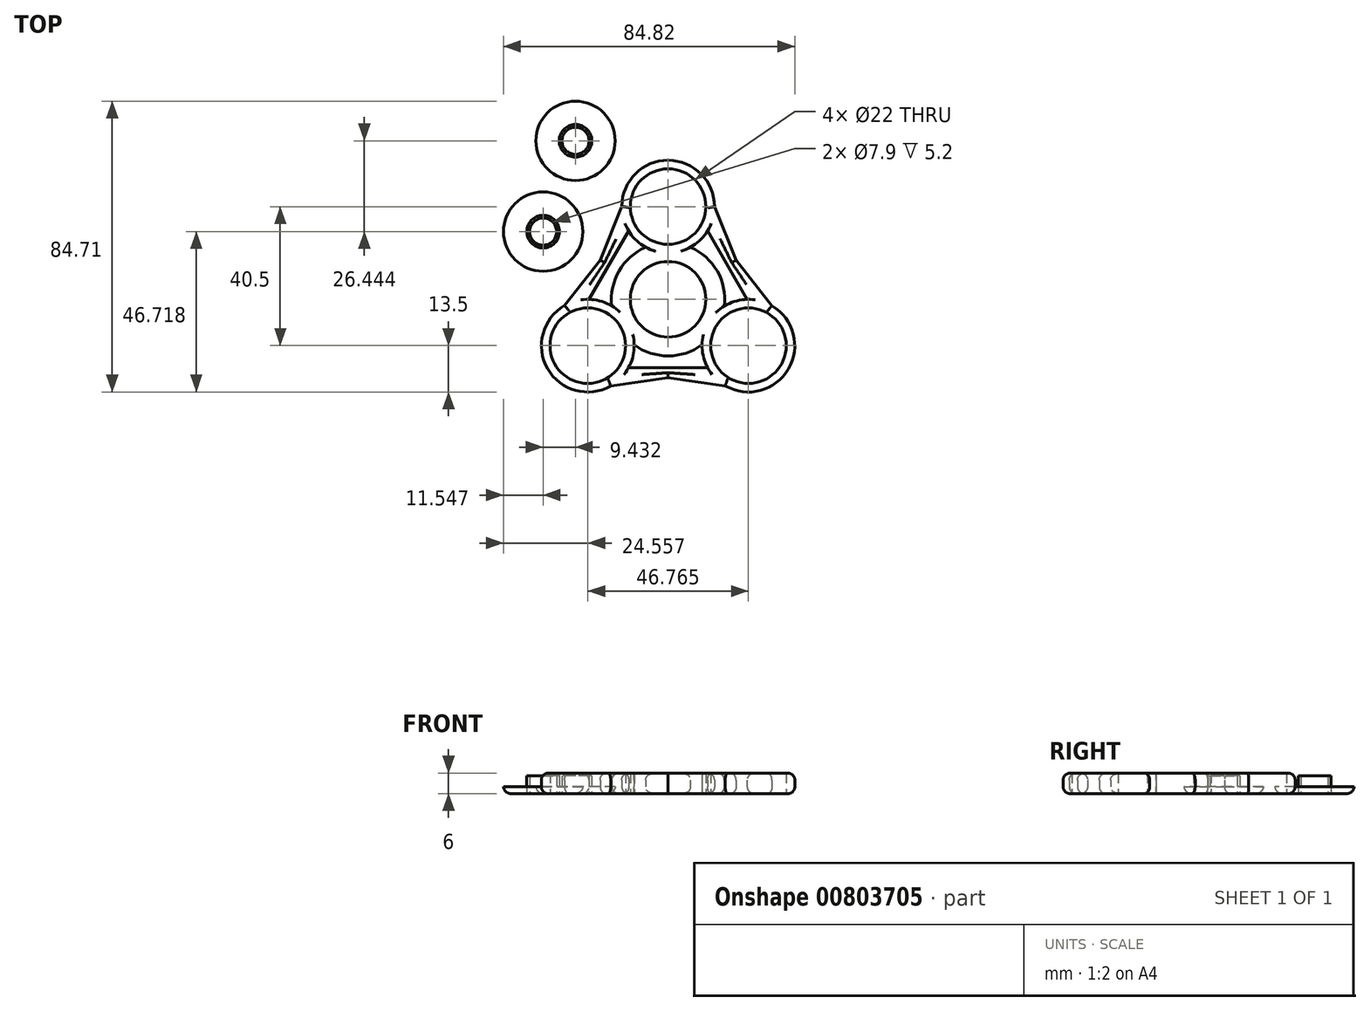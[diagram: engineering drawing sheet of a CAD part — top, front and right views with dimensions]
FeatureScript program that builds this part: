
annotation { "Feature Type Name" : "Feature", "Feature Type Description" : "" }
export const myFeature = defineFeature(function(context is Context, id is Id, definition is map)
    precondition{}
    {
        {
            var Q0;
            Q0=qCreatedBy(makeId("Top.planeOp"),FACE);
            var sketch = newSketch(context, id + "F0", { "sketchPlane" : qUnion([Q0])});
            skCircle(sketch, "E0", {"center": v(0, 0) * mm, "radius": 11 * mm});
            skArc(sketch, "E1", {"start": v(-6.5, 15.17) * mm, "mid": v(-14.29, 8.25) * mm, "end": v(-16.38, -1.96) * mm});
            skCircle(sketch, "E2", {"center": v(0, 27) * mm, "radius": 11 * mm});
            skArc(sketch, "E3", {"start": v(6.5, 15.17) * mm, "mid": v(9.3, 17.22) * mm, "end": v(11.5, 19.92) * mm});
            skLineSegment(sketch, "E4", {"start": v(-13.5, 27.1) * mm, "end": v(-19.78, 11.42) * mm});
            skLineSegment(sketch, "E5", {"start": v(-11.5, 19.92) * mm, "end": v(-17.25, 9.96) * mm});
            skLineSegment(sketch, "E6", {"start": v(13.5, 27) * mm, "end": v(19.78, 11.42) * mm});
            skLineSegment(sketch, "E7", {"start": v(11.5, 19.92) * mm, "end": v(17.25, 9.96) * mm});
            skArc(sketch, "E8.trimOffspring", {"start": v(13.5, 27) * mm, "mid": v(0.05, 40.5) * mm, "end": v(-13.5, 27.1) * mm});
            skArc(sketch, "E9.trimOffspring", {"start": v(-11.5, 19.92) * mm, "mid": v(-9.3, 17.22) * mm, "end": v(-6.5, 15.17) * mm});
            skArc(sketch, "E10.1.0", {"start": v(-30.13, -1.8) * mm, "mid": v(-35.1, -20.2) * mm, "end": v(-16.72, -25.24) * mm});
            skLineSegment(sketch, "E10.1.1", {"start": v(-30.13, -1.8) * mm, "end": v(-19.78, 11.42) * mm});
            skLineSegment(sketch, "E10.1.2", {"start": v(-23, 0) * mm, "end": v(-17.25, 9.96) * mm});
            skArc(sketch, "E10.1.3", {"start": v(-16.38, -1.96) * mm, "mid": v(-19.57, -0.55) * mm, "end": v(-23, 0) * mm});
            skArc(sketch, "E10.1.4", {"start": v(-11.5, -19.92) * mm, "mid": v(-10.26, -16.67) * mm, "end": v(-9.89, -13.21) * mm});
            skLineSegment(sketch, "E10.1.5", {"start": v(-11.5, -19.92) * mm, "end": v(0, -19.92) * mm});
            skLineSegment(sketch, "E10.1.6", {"start": v(-16.72, -25.24) * mm, "end": v(0, -22.84) * mm});
            skCircle(sketch, "E10.1.7", {"center": v(-23.38, -13.5) * mm, "radius": 11 * mm});
            skArc(sketch, "E10.2.0", {"start": v(16.63, -25.2) * mm, "mid": v(35.05, -20.3) * mm, "end": v(30.22, -1.86) * mm});
            skLineSegment(sketch, "E10.2.1", {"start": v(16.63, -25.2) * mm, "end": v(0, -22.84) * mm});
            skLineSegment(sketch, "E10.2.2", {"start": v(11.5, -19.92) * mm, "end": v(0, -19.92) * mm});
            skArc(sketch, "E10.2.3", {"start": v(9.89, -13.21) * mm, "mid": v(10.26, -16.67) * mm, "end": v(11.5, -19.92) * mm});
            skArc(sketch, "E10.2.4", {"start": v(23, 0) * mm, "mid": v(19.57, -0.55) * mm, "end": v(16.38, -1.96) * mm});
            skLineSegment(sketch, "E10.2.5", {"start": v(23, 0) * mm, "end": v(17.25, 9.96) * mm});
            skLineSegment(sketch, "E10.2.6", {"start": v(30.22, -1.86) * mm, "end": v(19.78, 11.42) * mm});
            skCircle(sketch, "E10.2.7", {"center": v(23.38, -13.5) * mm, "radius": 11 * mm});
            skPoint(sketch, "E11.orphan", {"position": v(-39.56, 22.84) * mm});
            skArc(sketch, "E12.trimOffspring", {"start": v(-9.89, -13.21) * mm, "mid": v(0, -16.5) * mm, "end": v(9.89, -13.21) * mm});
            skArc(sketch, "E13.trimOffspring", {"start": v(16.38, -1.96) * mm, "mid": v(14.29, 8.25) * mm, "end": v(6.5, 15.17) * mm});
            skSolve(sketch);
        }
        {
            var Q0;
            Q0 = qSketchRegion(id + "F0", true);
            extrude(context, id + "F1", {"entities" : qUnion([Q0]), "depth" : 6 * mm, "offsetDistance" : 25 * mm});
        }
        {
            var Q0;
            Q0=makeQuery(id+"F1.opExtrude","CAP_EDGE",EDGE,{"disambiguationData":[OSD([sQuery(id+"F0.wireOp",EDGE,"E10.1.6")])],"isStart":false});
            var Q1;
            Q1=makeQuery(id+"F1.opExtrude","CAP_EDGE",EDGE,{"disambiguationData":[OSD([sQuery(id+"F0.wireOp",EDGE,"E10.2.1")])],"isStart":false});
            var Q2;
            Q2=makeQuery(id+"F1.opExtrude","CAP_EDGE",EDGE,{"disambiguationData":[OSD([sQuery(id+"F0.wireOp",EDGE,"E10.2.6")])],"isStart":false});
            var Q3;
            Q3=makeQuery(id+"F1.opExtrude","CAP_EDGE",EDGE,{"disambiguationData":[OSD([sQuery(id+"F0.wireOp",EDGE,"E6")])],"isStart":false});
            var Q4;
            Q4=makeQuery(id+"F1.opExtrude","CAP_EDGE",EDGE,{"disambiguationData":[OSD([sQuery(id+"F0.wireOp",EDGE,"E10.1.1")])],"isStart":false});
            var Q5;
            Q5=makeQuery(id+"F1.opExtrude","CAP_EDGE",EDGE,{"disambiguationData":[OSD([sQuery(id+"F0.wireOp",EDGE,"E4")])],"isStart":false});
            var Q6;
            Q6=makeQuery(id+"F1.opExtrude","CAP_EDGE",EDGE,{"disambiguationData":[OSD([sQuery(id+"F0.wireOp",EDGE,"E10.1.1")])],"isStart":true});
            var Q7;
            Q7=makeQuery(id+"F1.opExtrude","CAP_EDGE",EDGE,{"disambiguationData":[OSD([sQuery(id+"F0.wireOp",EDGE,"E4")])],"isStart":true});
            var Q8;
            Q8=makeQuery(id+"F1.opExtrude","CAP_EDGE",EDGE,{"disambiguationData":[OSD([sQuery(id+"F0.wireOp",EDGE,"E10.1.6")])],"isStart":true});
            var Q9;
            Q9=makeQuery(id+"F1.opExtrude","CAP_EDGE",EDGE,{"disambiguationData":[OSD([sQuery(id+"F0.wireOp",EDGE,"E10.2.1")])],"isStart":true});
            var Q10;
            Q10=makeQuery(id+"F1.opExtrude","CAP_EDGE",EDGE,{"disambiguationData":[OSD([sQuery(id+"F0.wireOp",EDGE,"E10.2.6")])],"isStart":true});
            var Q11;
            Q11=makeQuery(id+"F1.opExtrude","CAP_EDGE",EDGE,{"disambiguationData":[OSD([sQuery(id+"F0.wireOp",EDGE,"E6")])],"isStart":true});
            var Q12;
            Q12=makeQuery(id+"F1.opExtrude","CAP_EDGE",EDGE,{"disambiguationData":[OSD([sQuery(id+"F0.wireOp",EDGE,"E10.1.0")])],"isStart":false});
            var Q13;
            Q13=makeQuery(id+"F1.opExtrude","CAP_EDGE",EDGE,{"disambiguationData":[OSD([sQuery(id+"F0.wireOp",EDGE,"E10.1.0")])],"isStart":true});
            var Q14;
            Q14=makeQuery(id+"F1.opExtrude","CAP_EDGE",EDGE,{"disambiguationData":[OSD([sQuery(id+"F0.wireOp",EDGE,"E8.trimOffspring")])],"isStart":false});
            var Q15;
            Q15=makeQuery(id+"F1.opExtrude","CAP_EDGE",EDGE,{"disambiguationData":[OSD([sQuery(id+"F0.wireOp",EDGE,"E8.trimOffspring")])],"isStart":true});
            var Q16;
            Q16=makeQuery(id+"F1.opExtrude","CAP_EDGE",EDGE,{"disambiguationData":[OSD([sQuery(id+"F0.wireOp",EDGE,"E10.2.0")])],"isStart":false});
            var Q17;
            Q17=makeQuery(id+"F1.opExtrude","CAP_EDGE",EDGE,{"disambiguationData":[OSD([sQuery(id+"F0.wireOp",EDGE,"E10.2.0")])],"isStart":true});
            var Q18;
            Q18=makeQuery(id+"F1.opExtrude","CAP_EDGE",EDGE,{"disambiguationData":[OSD([sQuery(id+"F0.wireOp",EDGE,"E12.trimOffspring")])],"isStart":true});
            var Q19;
            Q19=makeQuery(id+"F1.opExtrude","CAP_EDGE",EDGE,{"disambiguationData":[OSD([sQuery(id+"F0.wireOp",EDGE,"E13.trimOffspring")])],"isStart":true});
            var Q20;
            Q20=makeQuery(id+"F1.opExtrude","CAP_EDGE",EDGE,{"disambiguationData":[OSD([sQuery(id+"F0.wireOp",EDGE,"E1")])],"isStart":true});
            var Q21;
            Q21=makeQuery(id+"F1.opExtrude","CAP_EDGE",EDGE,{"disambiguationData":[OSD([sQuery(id+"F0.wireOp",EDGE,"E5"),sQuery(id+"F0.wireOp",EDGE,"E10.1.2")])],"isStart":true});
            var Q22;
            Q22=makeQuery(id+"F1.opExtrude","CAP_EDGE",EDGE,{"disambiguationData":[OSD([sQuery(id+"F0.wireOp",EDGE,"E7"),sQuery(id+"F0.wireOp",EDGE,"E10.2.5")])],"isStart":true});
            var Q23;
            Q23=makeQuery(id+"F1.opExtrude","CAP_EDGE",EDGE,{"disambiguationData":[OSD([sQuery(id+"F0.wireOp",EDGE,"E7"),sQuery(id+"F0.wireOp",EDGE,"E10.2.5")])],"isStart":false});
            var Q24;
            Q24=makeQuery(id+"F1.opExtrude","CAP_EDGE",EDGE,{"disambiguationData":[OSD([sQuery(id+"F0.wireOp",EDGE,"E10.1.5"),sQuery(id+"F0.wireOp",EDGE,"E10.2.2")])],"isStart":true});
            var Q25;
            Q25=makeQuery(id+"F1.opExtrude","CAP_EDGE",EDGE,{"disambiguationData":[OSD([sQuery(id+"F0.wireOp",EDGE,"E12.trimOffspring")])],"isStart":false});
            var Q26;
            Q26=makeQuery(id+"F1.opExtrude","CAP_EDGE",EDGE,{"disambiguationData":[OSD([sQuery(id+"F0.wireOp",EDGE,"E1")])],"isStart":false});
            var Q27;
            Q27=makeQuery(id+"F1.opExtrude","CAP_EDGE",EDGE,{"disambiguationData":[OSD([sQuery(id+"F0.wireOp",EDGE,"E10.1.5"),sQuery(id+"F0.wireOp",EDGE,"E10.2.2")])],"isStart":false});
            var Q28;
            Q28=makeQuery(id+"F1.opExtrude","CAP_EDGE",EDGE,{"disambiguationData":[OSD([sQuery(id+"F0.wireOp",EDGE,"E5"),sQuery(id+"F0.wireOp",EDGE,"E10.1.2")])],"isStart":false});
            var Q29;
            Q29=makeQuery(id+"F1.opExtrude","CAP_EDGE",EDGE,{"disambiguationData":[OSD([sQuery(id+"F0.wireOp",EDGE,"E13.trimOffspring")])],"isStart":false});
            fillet(context, id + "F2", {"entities" : qUnion([Q0, Q1, Q2, Q3, Q4, Q5, Q6, Q7, Q8, Q9, Q10, Q11, Q12, Q13, Q14, Q15, Q16, Q17, Q18, Q19, Q20, Q21, Q22, Q23, Q24, Q25, Q26, Q27, Q28, Q29]), "radius" : 2 * mm, "tangentPropagation" : true, "allowEdgeOverflow" : false});
        }
        {
            var Q0;
            Q0=qCreatedBy(makeId("Top.planeOp"),FACE);
            var sketch = newSketch(context, id + "F3", { "sketchPlane" : qUnion([Q0])});
            skCircle(sketch, "E14", {"center": v(-36.4, 19.72) * mm, "radius": 3.95 * mm});
            skCircle(sketch, "E15", {"center": v(-36.4, 19.72) * mm, "radius": 11.55 * mm});
            skCircle(sketch, "E16", {"center": v(-26.96, 46.16) * mm, "radius": 3.95 * mm});
            skCircle(sketch, "E17", {"center": v(-26.96, 46.16) * mm, "radius": 11.55 * mm});
            skCircle(sketch, "E18", {"center": v(-36.4, 19.72) * mm, "radius": 4.75 * mm});
            skCircle(sketch, "E19", {"center": v(-26.96, 46.16) * mm, "radius": 4.75 * mm});
            skSolve(sketch);
        }
        {
            var Q0;
            Q0=makeQuery(id+"F3.imprint","IMPRINT",FACE,{"disambiguationData":[TD([[makeQuery(id+"F3.imprint","IMPRINT",EDGE,{"derivedFrom":sQuery(id+"F3.wireOp",EDGE,"E15")}),1.0]])]});
            var Q1;
            Q1=makeQuery(id+"F3.imprint","IMPRINT",FACE,{"disambiguationData":[TD([[makeQuery(id+"F3.imprint","IMPRINT",EDGE,{"derivedFrom":sQuery(id+"F3.wireOp",EDGE,"E14")}),1.0]])]});
            var Q2;
            Q2=makeQuery(id+"F3.imprint","IMPRINT",FACE,{"disambiguationData":[TD([[makeQuery(id+"F3.imprint","IMPRINT",EDGE,{"derivedFrom":sQuery(id+"F3.wireOp",EDGE,"E14")}),-1.0]])]});
            var Q3;
            Q3=makeQuery(id+"F3.imprint","IMPRINT",FACE,{"disambiguationData":[TD([[makeQuery(id+"F3.imprint","IMPRINT",EDGE,{"derivedFrom":sQuery(id+"F3.wireOp",EDGE,"E17")}),1.0]])]});
            var Q4;
            Q4=makeQuery(id+"F3.imprint","IMPRINT",FACE,{"disambiguationData":[TD([[makeQuery(id+"F3.imprint","IMPRINT",EDGE,{"derivedFrom":sQuery(id+"F3.wireOp",EDGE,"E16")}),1.0]])]});
            var Q5;
            Q5=makeQuery(id+"F3.imprint","IMPRINT",FACE,{"disambiguationData":[TD([[makeQuery(id+"F3.imprint","IMPRINT",EDGE,{"derivedFrom":sQuery(id+"F3.wireOp",EDGE,"E16")}),-1.0]])]});
            extrude(context, id + "F4", {"entities" : qUnion([Q0, Q1, Q2, Q3, Q4, Q5]), "depth" : 2 * mm, "offsetDistance" : 25 * mm});
        }
        {
            var Q0;
            Q0=makeQuery(id+"F3.imprint","IMPRINT",FACE,{"disambiguationData":[TD([[makeQuery(id+"F3.imprint","IMPRINT",EDGE,{"derivedFrom":sQuery(id+"F3.wireOp",EDGE,"E14")}),-1.0]])]});
            var Q1;
            Q1=makeQuery(id+"F3.imprint","IMPRINT",FACE,{"disambiguationData":[TD([[makeQuery(id+"F3.imprint","IMPRINT",EDGE,{"derivedFrom":sQuery(id+"F3.wireOp",EDGE,"E16")}),-1.0]])]});
            extrude(context, id + "F5", {"entities" : qUnion([Q0, Q1]), "depth" : 5.2 * mm, "offsetDistance" : 25 * mm});
        }
        {
            var Q0;
            Q0=makeQuery(id+"F4.opExtrude","CAP_EDGE",EDGE,{"disambiguationData":[OSD([sQuery(id+"F3.wireOp",EDGE,"E17")])],"isStart":true});
            var Q1;
            Q1=makeQuery(id+"F4.opExtrude","CAP_EDGE",EDGE,{"disambiguationData":[OSD([sQuery(id+"F3.wireOp",EDGE,"E15")])],"isStart":true});
            fillet(context, id + "F6", {"entities" : qUnion([Q0, Q1]), "radius" : 2.3 * mm, "tangentPropagation" : true, "allowEdgeOverflow" : false});
        }
    });
